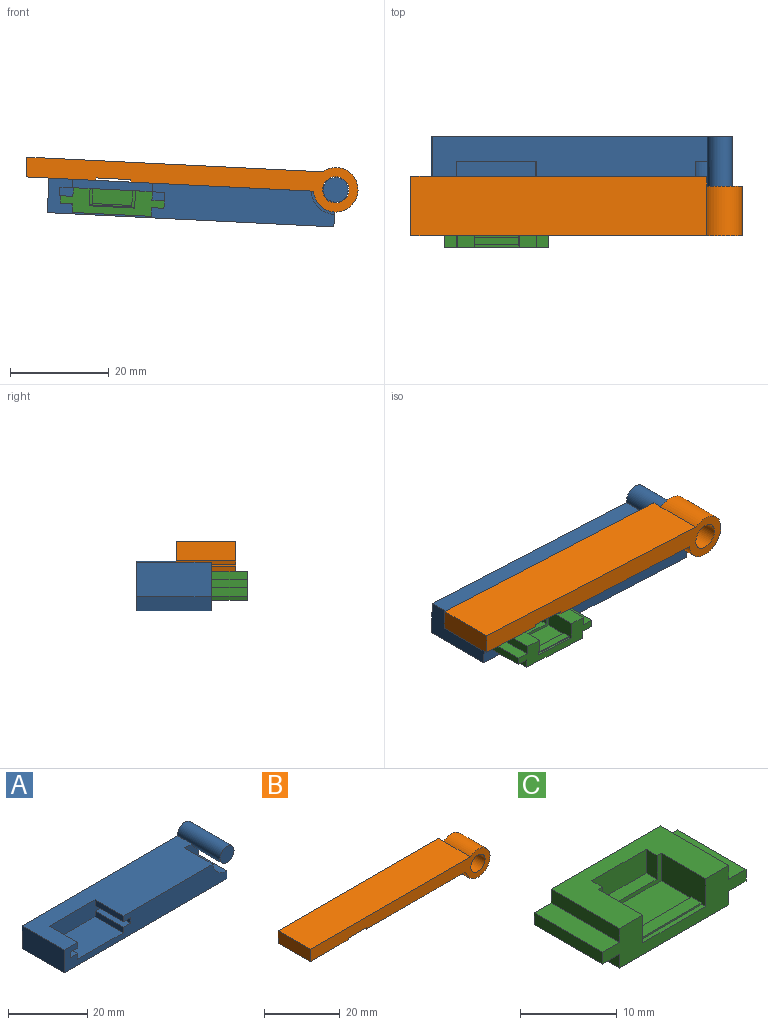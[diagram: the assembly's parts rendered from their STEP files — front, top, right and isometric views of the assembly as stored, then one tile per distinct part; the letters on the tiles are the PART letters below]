
ASSEMBLY  parts=3 mates=2
PART A: 22 faces, bbox 60.5x15x10 mm
  f0: plane 5x5mm, normal (0,-1,0), area 19.6mm2, adj f19
  f1: plane 10x1.75mm, normal (1,0,0), area 17.5mm2, adj f3,f4,f12,f14
  f2: plane 10x1.75mm, normal (-1,0,0), area 17.5mm2, adj f3,f4,f12,f18
  f3: plane 58x7mm, normal (0,-1,0), area 296.1mm2, adj f1,f2,f4,f5,f7,f8,f9,f10
  f4: plane 55.55x15mm, normal (0,0,1), area 646mm2, adj f1,f2,f3,f6,f7,f12,f19,f20
  f5: plane 15x5mm, normal (1,0,0), area 50mm2, adj f3,f6,f8,f19,f20,f21
  f6: plane 60.5x10mm, normal (0,1,0), area 422mm2, adj f4,f5,f7,f8,f19
  f7: plane 15x7mm, normal (-1,0,0), area 105mm2, adj f3,f4,f6,f8
  f8: plane 58x15mm, normal (0,0,-1), area 870mm2, adj f3,f5,f6,f7
  f9: plane 10x1.75mm, normal (1,0,0), area 17.5mm2, adj f3,f10,f12,f13
  f10: plane 16.2x10mm, normal (0,0,1), area 162mm2, adj f3,f9,f11,f12
  f11: plane 10x1.75mm, normal (-1,0,0), area 17.5mm2, adj f3,f10,f12,f16
  f12: plane 21.2x5.2mm, normal (0,-1,0), area 92.7mm2, adj f1,f2,f4,f9,f10,f11,f13,f14
  f13: plane 10x2.5mm, normal (0,0,1), area 25mm2, adj f3,f9,f12,f15
  f14: plane 10x2.5mm, normal (0,0,-1), area 25mm2, adj f1,f3,f12,f15
  f15: plane 10x1.7mm, normal (1,0,0), area 17mm2, adj f3,f12,f13,f14
  f16: plane 10x2.5mm, normal (0,0,1), area 25mm2, adj f3,f11,f12,f17
  f17: plane 10x1.7mm, normal (-1,0,0), area 17mm2, adj f3,f12,f16,f18
  f18: plane 10x2.5mm, normal (0,0,-1), area 25mm2, adj f2,f3,f12,f17
  f19: cylinder r=2.5mm len=15mm, axis (0,-1,0), area 218.5mm2, adj f0,f4,f5,f6,f21
  f20: cylinder r=5mm len=10mm, axis (0,-1,0), area 73.5mm2, adj f3,f4,f5,f21
  f21: plane 4.98x4.5mm, normal (0,-1,0), area 13.5mm2, adj f4,f5,f19,f20
PART B: 13 faces, bbox 67.2x12x9 mm
  f0: plane 14.15x12mm, normal (0,0,-1), area 169.8mm2, adj f1,f7,f8,f9
  f1: plane 67.15x9mm, normal (0,-1,0), area 272.4mm2, adj f0,f2,f3,f6,f7,f9,f10,f11
  f2: cylinder r=4.5mm len=10mm, axis (0,1,0), area 237.6mm2, adj f1,f4,f6,f12
  f3: cylinder r=2.65mm len=10mm, axis (0,1,0), area 166.5mm2, adj f1,f4
  f4: plane 9x9mm, normal (0,1,0), area 41.6mm2, adj f2,f3,f5
  f5: cylinder r=4.5mm len=4mm, axis (0,-1,0), area 9mm2, adj f4,f6,f8,f12
  f6: plane 37.03x12mm, normal (0,0,-1), area 444.3mm2, adj f1,f2,f5,f8,f10
  f7: plane 12x4mm, normal (-1,0,0), area 48mm2, adj f0,f1,f8,f12
  f8: plane 59.82x4mm, normal (0,1,0), area 230.9mm2, adj f0,f5,f6,f7,f9,f10,f11,f12
  f9: plane 12x0.5mm, normal (1,0,0), area 6mm2, adj f0,f1,f8,f11
  f10: plane 12x0.5mm, normal (-1,0,0), area 6mm2, adj f1,f6,f8,f11
  f11: plane 12x7mm, normal (0,0,-1), area 84mm2, adj f1,f8,f9,f10
  f12: plane 59.82x12mm, normal (0,0,1), area 717.9mm2, adj f1,f2,f5,f7,f8
PART C: 26 faces, bbox 21x10x5 mm
  f0: plane 10x1.75mm, normal (1,0,0), area 17.5mm2, adj f5,f10,f12,f23
  f1: plane 10x1.75mm, normal (-1,0,0), area 17.5mm2, adj f5,f10,f12,f20
  f2: plane 9.2x0.53mm, normal (0,0,1), area 4.9mm2, adj f3,f5,f7,f18
  f3: plane 6.51x3.5mm, normal (1,0,0), area 22.5mm2, adj f2,f4,f5,f8,f13,f17,f18,f19
  f4: plane 16x10mm, normal (0,0,1), area 87.5mm2, adj f3,f5,f6,f7,f9,f10,f11,f13
  f5: plane 21x5mm, normal (0,-1,0), area 55.3mm2, adj f0,f1,f2,f3,f4,f7,f9,f11
  f6: plane 8x3mm, normal (0,-1,0), area 24mm2, adj f4,f14,f15,f16
  f7: plane 6.51x3.5mm, normal (-1,0,0), area 22.5mm2, adj f2,f4,f5,f8,f13,f17,f18,f19
  f8: plane 9.2x4.48mm, normal (0,0,1), area 41.2mm2, adj f3,f7,f13,f17
  f9: plane 10x1.75mm, normal (1,0,0), area 17.5mm2, adj f4,f5,f10,f24
  f10: plane 21x5mm, normal (0,1,0), area 87.5mm2, adj f0,f1,f4,f9,f11,f12,f20,f21
  f11: plane 10x1.75mm, normal (-1,0,0), area 17.5mm2, adj f4,f5,f10,f21
  f12: plane 16x10mm, normal (0,0,-1), area 160mm2, adj f0,f1,f5,f10
  f13: plane 9.2x3.5mm, normal (0,-1,0), area 8.2mm2, adj f3,f4,f7,f8,f14,f15,f16
  f14: plane 8x1.57mm, normal (0,0,1), area 12.6mm2, adj f6,f13,f15,f16
  f15: plane 3x1.57mm, normal (-1,0,0), area 4.7mm2, adj f4,f6,f13,f14
  f16: plane 3x1.57mm, normal (1,0,0), area 4.7mm2, adj f4,f6,f13,f14
  f17: plane 9.2x0.2mm, normal (0,1,0), area 1.8mm2, adj f3,f7,f8,f19
  f18: plane 9.2x0.2mm, normal (0,-1,0), area 1.8mm2, adj f2,f3,f7,f19
  f19: plane 9.2x1.5mm, normal (0,0,1), area 13.8mm2, adj f3,f7,f17,f18
  f20: plane 10x2.5mm, normal (0,0,-1), area 25mm2, adj f1,f5,f10,f22
  f21: plane 10x2.5mm, normal (0,0,1), area 25mm2, adj f5,f10,f11,f22
  f22: plane 10x1.5mm, normal (-1,0,0), area 15mm2, adj f5,f10,f20,f21
  f23: plane 10x2.5mm, normal (0,0,-1), area 25mm2, adj f0,f5,f10,f25
  f24: plane 10x2.5mm, normal (0,0,1), area 25mm2, adj f5,f9,f10,f25
  f25: plane 10x1.5mm, normal (1,0,0), area 15mm2, adj f5,f10,f23,f24
PLACE A rot(axis=(0,1,0),2.8deg) t=(-0.76,3,0.77)mm
PLACE B rot(axis=(0,1,0),2.8deg) t=(28.58,0.5,6.83)mm
PLACE C rot(axis=(0,1,0),2.8deg) t=(-16.72,-6.8,1.86)mm
MATE planar C.f25 <-> A.f17  axis (1,0,-0.05) through (-6.11,-1.8,3.84)mm
MATE revolute A.f19 <-> B.f2  axis (0,-1,0) through (28.58,-4.5,6.83)mm
